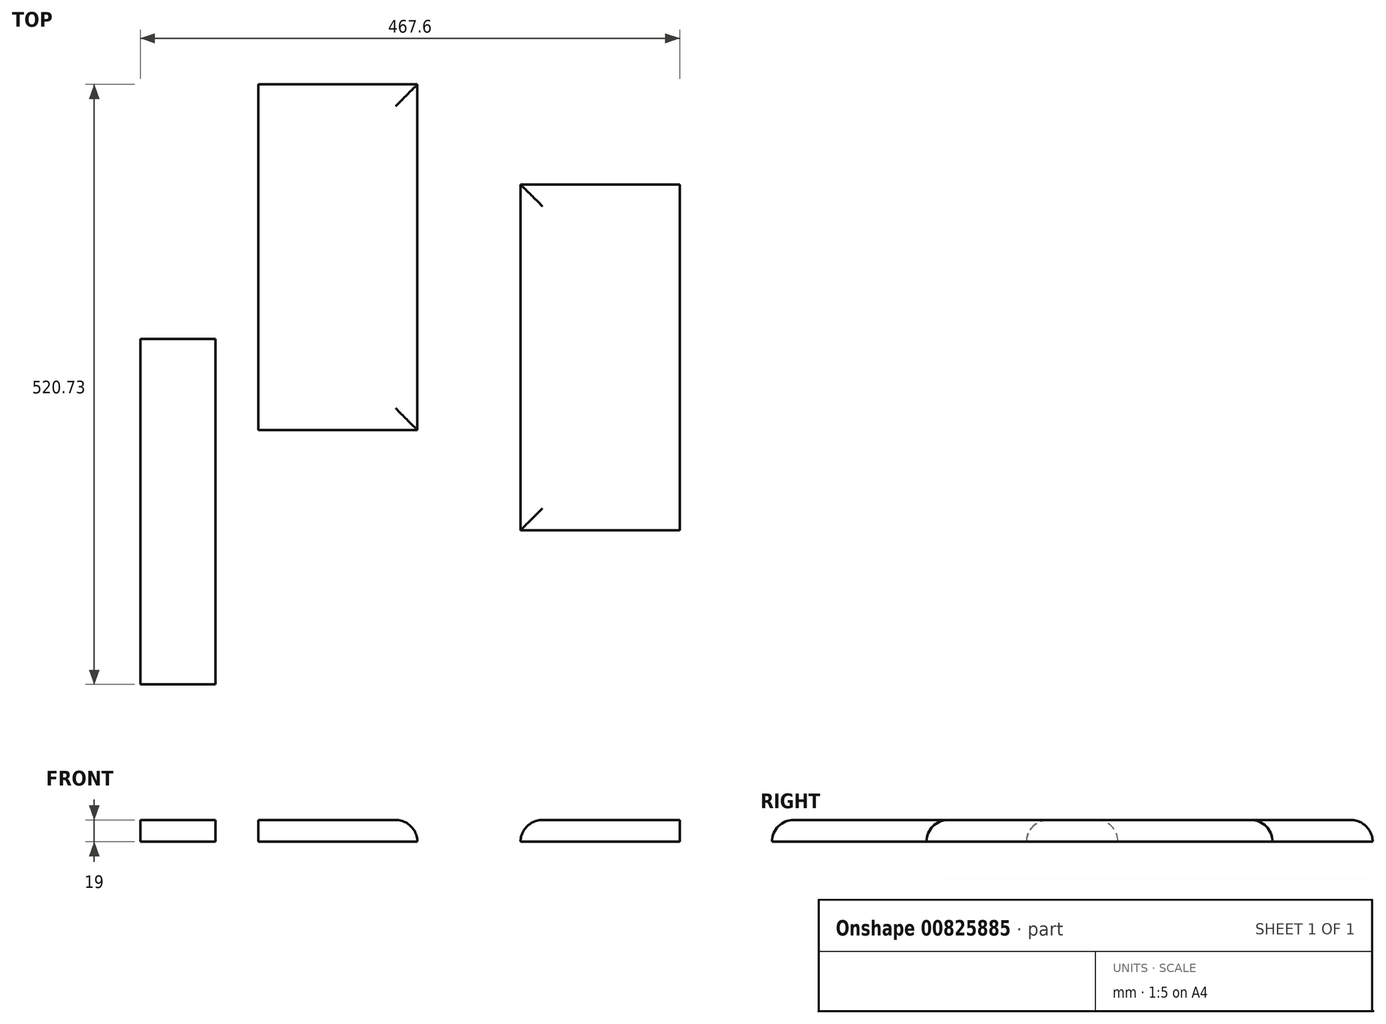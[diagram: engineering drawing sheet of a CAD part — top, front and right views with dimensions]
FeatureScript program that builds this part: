
annotation { "Feature Type Name" : "Feature", "Feature Type Description" : "" }
export const myFeature = defineFeature(function(context is Context, id is Id, definition is map)
    precondition{}
    {
        {
            var Q0;
            Q0=qCreatedBy(makeId("Top.planeOp"),FACE);
            var sketch = newSketch(context, id + "F0", { "sketchPlane" : qUnion([Q0])});
            skLineSegment(sketch, "E0.bottom", {"start": v(-146.23, 220.73) * mm, "end": v(-8.23, 220.73) * mm});
            skLineSegment(sketch, "E0.top", {"start": v(-146.23, -79.27) * mm, "end": v(-8.23, -79.27) * mm});
            skLineSegment(sketch, "E0.left", {"start": v(-146.23, 220.73) * mm, "end": v(-146.23, -79.27) * mm});
            skLineSegment(sketch, "E0.right", {"start": v(-8.23, 220.73) * mm, "end": v(-8.23, -79.27) * mm});
            skSolve(sketch);
        }
        {
            var Q0;
            Q0=makeQuery(id+"F0.imprint","IMPRINT",FACE,{"disambiguationData":[TD([[makeQuery(id+"F0.imprint","IMPRINT",EDGE,{"derivedFrom":sQuery(id+"F0.wireOp",EDGE,"E0.bottom")}),-1.0]])]});
            extrude(context, id + "F1", {"entities" : qUnion([Q0]), "depth" : 19 * mm, "offsetDistance" : 25 * mm});
        }
        {
            var Q0;
            Q0=qCreatedBy(makeId("Top.planeOp"),FACE);
            var sketch = newSketch(context, id + "F2", { "sketchPlane" : qUnion([Q0])});
            skLineSegment(sketch, "E1.bottom", {"start": v(-248.35, 0) * mm, "end": v(-183.35, 0) * mm});
            skLineSegment(sketch, "E1.top", {"start": v(-248.35, -300) * mm, "end": v(-183.35, -300) * mm});
            skLineSegment(sketch, "E1.left", {"start": v(-248.35, 0) * mm, "end": v(-248.35, -300) * mm});
            skLineSegment(sketch, "E1.right", {"start": v(-183.35, 0) * mm, "end": v(-183.35, -300) * mm});
            skSolve(sketch);
        }
        {
            var Q0;
            Q0=qSketchRegion(id+"F2",true);
            extrude(context, id + "F3", {"entities" : qUnion([Q0]), "depth" : 19 * mm, "offsetDistance" : 25 * mm});
        }
        {
            var Q0;
            Q0=qCreatedBy(makeId("Top.planeOp"),FACE);
            var sketch = newSketch(context, id + "F4", { "sketchPlane" : qUnion([Q0])});
            skLineSegment(sketch, "E2.bottom", {"start": v(81.25, 133.92) * mm, "end": v(219.25, 133.92) * mm});
            skLineSegment(sketch, "E2.top", {"start": v(81.25, -166.08) * mm, "end": v(219.25, -166.08) * mm});
            skLineSegment(sketch, "E2.left", {"start": v(81.25, 133.92) * mm, "end": v(81.25, -166.08) * mm});
            skLineSegment(sketch, "E2.right", {"start": v(219.25, 133.92) * mm, "end": v(219.25, -166.08) * mm});
            skSolve(sketch);
        }
        {
            var Q0;
            Q0=qSketchRegion(id+"F4",true);
            extrude(context, id + "F5", {"entities" : qUnion([Q0]), "depth" : 19 * mm, "offsetDistance" : 25 * mm});
        }
        {
            var Q0;
            Q0=makeQuery(id+"F3.opExtrude","CAP_EDGE",EDGE,{"disambiguationData":[OSD([sQuery(id+"F2.wireOp",EDGE,"E1.bottom")])],"isStart":false});
            var Q1;
            Q1=makeQuery(id+"F3.opExtrude","CAP_EDGE",EDGE,{"disambiguationData":[OSD([sQuery(id+"F2.wireOp",EDGE,"E1.top")])],"isStart":false});
            var Q2;
            Q2=makeQuery(id+"F1.opExtrude","CAP_EDGE",EDGE,{"disambiguationData":[OSD([sQuery(id+"F0.wireOp",EDGE,"E0.top")])],"isStart":false});
            var Q3;
            Q3=makeQuery(id+"F1.opExtrude","CAP_EDGE",EDGE,{"disambiguationData":[OSD([sQuery(id+"F0.wireOp",EDGE,"E0.right")])],"isStart":false});
            var Q4;
            Q4=makeQuery(id+"F1.opExtrude","CAP_EDGE",EDGE,{"disambiguationData":[OSD([sQuery(id+"F0.wireOp",EDGE,"E0.bottom")])],"isStart":false});
            var Q5;
            Q5=makeQuery(id+"F5.opExtrude","CAP_EDGE",EDGE,{"disambiguationData":[OSD([sQuery(id+"F4.wireOp",EDGE,"E2.bottom")])],"isStart":false});
            var Q6;
            Q6=makeQuery(id+"F5.opExtrude","CAP_EDGE",EDGE,{"disambiguationData":[OSD([sQuery(id+"F4.wireOp",EDGE,"E2.left")])],"isStart":false});
            var Q7;
            Q7=makeQuery(id+"F5.opExtrude","CAP_EDGE",EDGE,{"disambiguationData":[OSD([sQuery(id+"F4.wireOp",EDGE,"E2.top")])],"isStart":false});
            fillet(context, id + "F6", {"entities" : qUnion([Q0, Q1, Q2, Q3, Q4, Q5, Q6, Q7]), "radius" : 19 * mm, "tangentPropagation" : true, "allowEdgeOverflow" : false});
        }
    });
